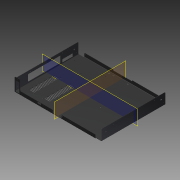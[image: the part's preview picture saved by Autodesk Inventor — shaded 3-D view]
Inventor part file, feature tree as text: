
AUTODESK INVENTOR PART (.ipt)
format: ipt  version: 2015 (Build 190159000, 159)  size: 830,464 bytes
history: native  units: mm
features: extrude x12, hole x10, reference x8, fillet x7, other x2, shell x1, pattern_linear x1
ambient origin geometry x8: Origin, YZ Plane, XZ Plane, XY Plane, X Axis, Y Axis, Z Axis, Center Point
bodies: Solid1 (feature_tree)
feature tree (41):
  extrude  "Extrusión1"  Depth=485.0mm
  fillet  "Empalme1"  Radius=364.0mm
  shell  "Vaciado1"  Thickness=60.0mm
  extrude  "Extrusión2"  Depth=5.0mm
  extrude  "Extrusión3"  Depth=3.0mm
  hole  "Agujero1"  [1 undecoded]
  extrude  "Extrusión4"  Depth=60.0mm TaperAngle=0.0deg
  fillet  "Empalme2"  Radius=50.0mm
  extrude  "Extrusión5"  Depth=35.0mm
  hole  "Agujero2"  [1 undecoded]
  hole  "Agujero3"  [1 undecoded]
  hole  "Agujero5"  [1 undecoded]
  hole  "Agujero6"  [1 undecoded]
  hole  "Agujero7"  [1 undecoded]
  extrude  "Extrusión6"  Depth=16.5mm
  pattern_linear  "Patrón rectangular1"  Spacing1=5.0mm  [1 undecoded]
  fillet  "Empalme3"  Radius=10.0mm
  hole  "RAMPS"  [1 undecoded]
  extrude  "Extrusión7"  Depth=105.0mm
  hole  "Agujero9"  [1 undecoded]
  hole  "Agujero10"  [1 undecoded]
  extrude  "Extrusión9"  Depth=35.5mm
  fillet  "Empalme4"  Radius=307.0mm
  extrude  "Extrusión10"  Depth=15.0mm
  other  "Desplazar cara1"
  extrude  "Extrusión11"  Depth=409.0mm
  fillet  "Empalme5"  Radius=31.0mm
  fillet  "Empalme6"  Radius=80.0mm
  hole  "Agujero11"  [1 undecoded]
  extrude  "Extrusión13"  Depth=50.0mm
  fillet  "Empalme7"  Radius=150.0mm
  extrude  "Extrusión14"  Depth=44.5mm
  reference  "Referencia5"
  reference  "Referencia6"
  reference  "Referencia7"
  reference  "Referencia8"
  reference  "Referencia9"
  reference  "Referencia10"
  reference  "Referencia11"
  reference  "Referencia12"
  other  "Definición1"
note: 11 required parameter values undecoded (feature->parameter linkage not recoverable at this tier; creation-order binding heuristic only, values carry confidence <= 0.55)
